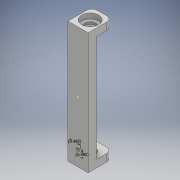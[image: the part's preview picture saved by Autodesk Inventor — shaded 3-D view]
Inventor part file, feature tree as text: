
AUTODESK INVENTOR PART (.ipt)
format: ipt  version: 2018 (Build 220112000, 112)  size: 223,232 bytes
history: native  units: mm
features: sketch x14, extrude x10, fillet x3
ambient origin geometry x8: Origin, YZ Plane, XZ Plane, XY Plane, X Axis, Y Axis, Z Axis, Center Point
bodies: Solid1 (feature_tree)
feature tree (27):
  extrude  "Extrusion1"  Depth=100.0mm
  sketch  "Sketch2"  dims[d2=2.0mm d3=0.0mm d4=2.5mm]
  sketch  "Sketch3"  dims[d5=2.5mm d6=10.89mm d7=0.0mm]
  extrude  "Extrusion2"  Depth=2.5mm
  extrude  "Extrusion3"  Depth=10.89mm TaperAngle=0.0deg
  extrude  "Extrusion4"  Depth=2.14mm TaperAngle=0.0deg
  extrude  "Extrusion5"  Depth=2.14mm TaperAngle=0.0deg
  fillet  "Fillet1"  Radius=7.0mm
  extrude  "Extrusion6"  Depth=22.5mm
  extrude  "Extrusion7"  Depth=7.0mm TaperAngle=0.0deg
  fillet  "Fillet2"  Radius=7.0mm
  extrude  "Extrusion8"  Depth=5.0mm
  extrude  "Extrusion9"  Depth=2.0mm TaperAngle=0.0deg
  sketch  "Sketch12"  dims[d33=2.0mm d34=0.0mm]
  extrude  "Extrusion10"  Depth=2.0mm TaperAngle=0.0deg
  fillet  "Fillet3"  Radius=13.97mm
  sketch  "Sketch14"  dims[d36=6.985mm d37=9.485mm]
  sketch  "Sketch1"  dims[d0=13.97mm d1=100.0mm]
  sketch  "Sketch4"  dims[d8=3.14mm d9=0.0mm d10=2.14mm d11=0.0mm]
  sketch  "Sketch5"  dims[d12=3.5mm d13=2.14mm d14=0.0mm d15=7.0mm]
  sketch  "Sketch6"  dims[d16=11.43mm d17=22.5mm]
  sketch  "Sketch7"  dims[d18=15.975mm d19=7.0mm d20=0.0mm d21=7.0mm d22=0.0mm]
  sketch  "Sketch8"  dims[d23=5.0mm d24=6.35mm]
  sketch  "Sketch9"  dims[d25=10.0mm d26=2.0mm d27=0.0mm]
  sketch  "Sketch10"  dims[d28=10.0mm d29=2.0mm d30=0.0mm d31=13.97mm]
  sketch  "Sketch11"  dims[d32=3.175mm]
  sketch  "Sketch13"  dims[d35=2.0mm]
